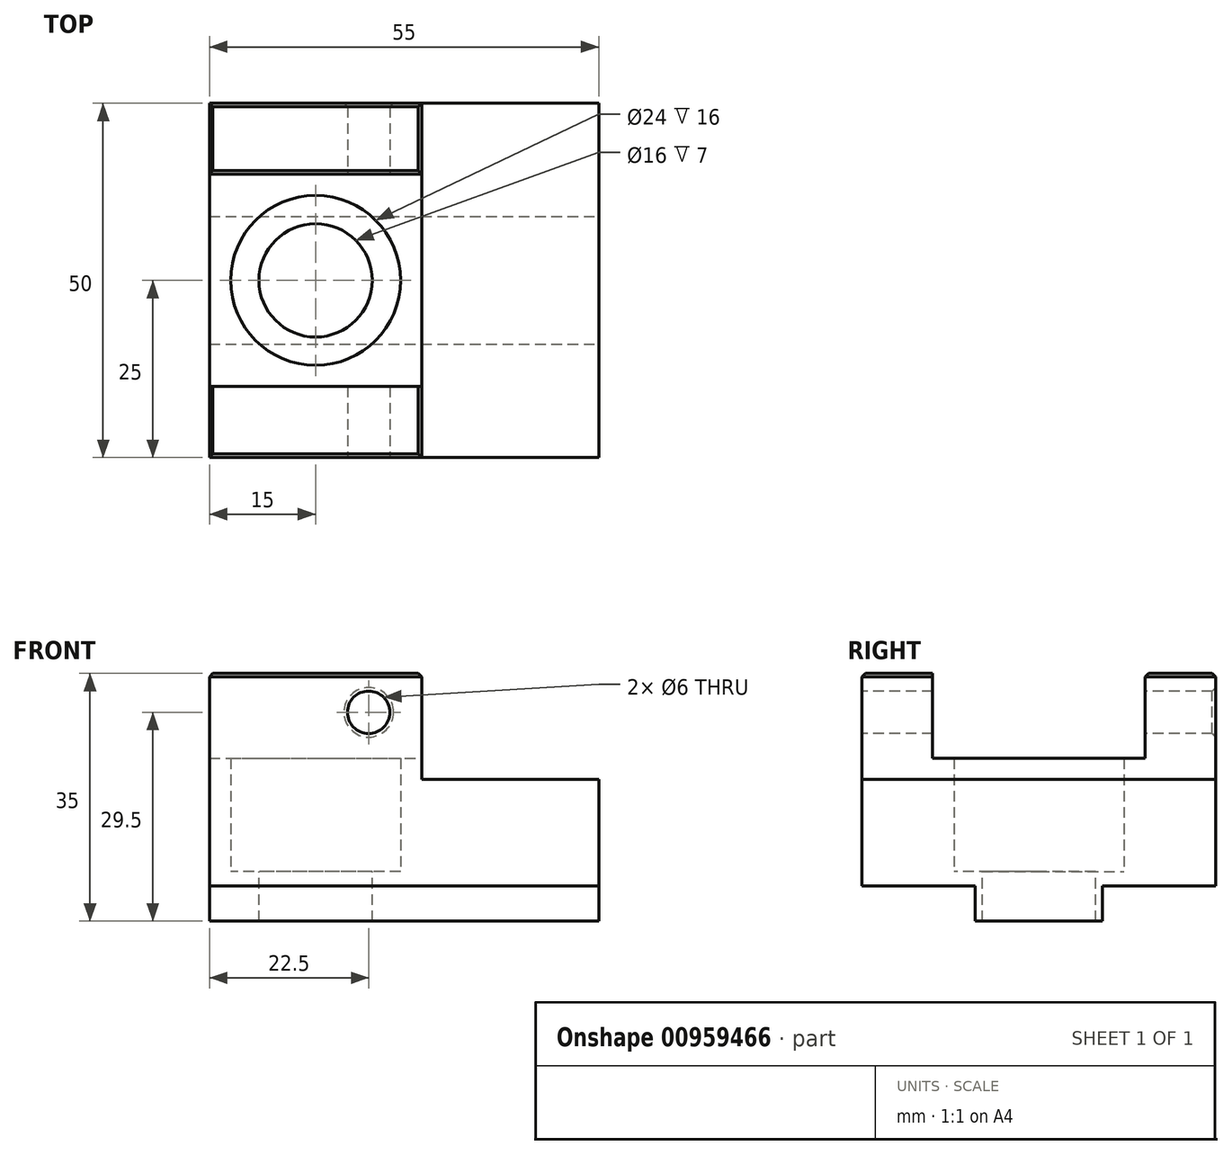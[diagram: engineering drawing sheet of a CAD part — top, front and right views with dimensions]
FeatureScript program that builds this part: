
annotation { "Feature Type Name" : "Feature", "Feature Type Description" : "" }
export const myFeature = defineFeature(function(context is Context, id is Id, definition is map)
    precondition{}
    {
        {
            var Q0;
            Q0=qCreatedBy(makeId("Top.planeOp"),FACE);
            var sketch = newSketch(context, id + "F0", { "sketchPlane" : qUnion([Q0])});
            skLineSegment(sketch, "E0.bottom", {"start": v(0, 0) * mm, "end": v(-30, 0) * mm});
            skLineSegment(sketch, "E0.top", {"start": v(0, 50) * mm, "end": v(-30, 50) * mm});
            skLineSegment(sketch, "E0.left", {"start": v(0, 0) * mm, "end": v(0, 50) * mm});
            skLineSegment(sketch, "E0.right", {"start": v(-30, 0) * mm, "end": v(-30, 50) * mm});
            skSolve(sketch);
        }
        {
            var Q0;
            Q0 = qSketchRegion(id + "F0", true);
            extrude(context, id + "F1", {"entities" : qUnion([Q0]), "depth" : 30 * mm, "offsetDistance" : 25 * mm});
        }
        {
            var Q0;
            Q0=makeQuery(id+"F1.opExtrude","SWEPT_FACE",FACE,{"disambiguationData":[OSD([sQuery(id+"F0.wireOp",EDGE,"E0.left")])]});
            var sketch = newSketch(context, id + "F2", { "sketchPlane" : qUnion([Q0])});
            skLineSegment(sketch, "E1.bottom", {"start": v(0, 0) * mm, "end": v(50, 0) * mm});
            skLineSegment(sketch, "E1.top", {"start": v(0, 15) * mm, "end": v(50, 15) * mm});
            skLineSegment(sketch, "E1.left", {"start": v(0, 0) * mm, "end": v(0, 15) * mm});
            skLineSegment(sketch, "E1.right", {"start": v(50, 0) * mm, "end": v(50, 15) * mm});
            skSolve(sketch);
        }
        {
            var Q0;
            Q0 = qSketchRegion(id + "F2", true);
            extrude(context, id + "F3", {"entities" : qUnion([Q0]), "operationType" : NewBodyOperationType.ADD, "depth" : 25 * mm, "offsetDistance" : 25 * mm});
        }
        {
            var Q0;
            Q0=makeQuery(id+"F3.boolean.opBoolean","MERGE",FACE,{"derivedFrom":[makeQuery(id+"F1.opExtrude","SWEPT_FACE",FACE,{"disambiguationData":[OSD([sQuery(id+"F0.wireOp",EDGE,"E0.bottom")])]}),makeQuery(id+"F3.opExtrude","SWEPT_FACE",FACE,{"disambiguationData":[OSD([sQuery(id+"F2.wireOp",EDGE,"E1.left")])]})]});
            var sketch = newSketch(context, id + "F4", { "sketchPlane" : qUnion([Q0])});
            skCircle(sketch, "E2", {"center": v(-7.5, 24.5) * mm, "radius": 3 * mm});
            skLineSegment(sketch, "E3", {"start": v(0, 15) * mm, "end": v(0, 30) * mm, "construction": true});
            skLineSegment(sketch, "E4", {"start": v(0, 24.5) * mm, "end": v(-30, 24.5) * mm, "construction": true});
            skSolve(sketch);
        }
        {
            var Q0;
            Q0=makeQuery(id+"F3.boolean.opBoolean","MERGE",FACE,{"derivedFrom":[makeQuery(id+"F1.opExtrude","CAP_FACE",FACE,{"disambiguationData":[OSD([sQuery(id+"F0.wireOp",EDGE,"E0.bottom"),sQuery(id+"F0.wireOp",EDGE,"E0.top"),sQuery(id+"F0.wireOp",EDGE,"E0.left"),sQuery(id+"F0.wireOp",EDGE,"E0.right")])],"isStart":true}),makeQuery(id+"F3.opExtrude","SWEPT_FACE",FACE,{"disambiguationData":[OSD([sQuery(id+"F2.wireOp",EDGE,"E1.bottom")])]})]});
            var sketch = newSketch(context, id + "F5", { "sketchPlane" : qUnion([Q0])});
            skLineSegment(sketch, "E5.bottom", {"start": v(-30, -16) * mm, "end": v(25, -16) * mm});
            skLineSegment(sketch, "E5.top", {"start": v(-30, -34) * mm, "end": v(25, -34) * mm});
            skLineSegment(sketch, "E5.left", {"start": v(-30, -16) * mm, "end": v(-30, -34) * mm});
            skLineSegment(sketch, "E5.right", {"start": v(25, -16) * mm, "end": v(25, -34) * mm});
            skLineSegment(sketch, "E6", {"start": v(-30, -25) * mm, "end": v(25, -25) * mm, "construction": true});
            skSolve(sketch);
        }
        {
            var Q0;
            Q0 = qSketchRegion(id + "F5", true);
            extrude(context, id + "F6", {"entities" : qUnion([Q0]), "operationType" : NewBodyOperationType.ADD, "depth" : 5 * mm, "offsetDistance" : 25 * mm});
        }
        {
            var Q0;
            Q0=makeQuery(id+"F4.imprint","IMPRINT",FACE,{"disambiguationData":[TD([[makeQuery(id+"F4.imprint","IMPRINT",EDGE,{"derivedFrom":sQuery(id+"F4.wireOp",EDGE,"E2")}),1.0]])]});
            extrude(context, id + "F7", {"entities" : qUnion([Q0]), "operationType" : NewBodyOperationType.REMOVE, "endBound" : BoundingType.THROUGH_ALL, "oppositeDirection" : true, "depth" : 25 * mm, "offsetDistance" : 25 * mm});
        }
        {
            var Q0;
            Q0=makeQuery(id+"F7.boolean.opBoolean","COPY",EDGE,{"derivedFrom":makeQuery(id+"F7.opExtrude","CAP_EDGE",EDGE,{"disambiguationData":[OSD([sQuery(id+"F4.wireOp",EDGE,"E2")])],"isStart":true})});
            var Q1;
            Q1=makeQuery(id+"F7.boolean.opBoolean","INTERSECT",EDGE,{"derivedFrom":[makeQuery(id+"F3.boolean.opBoolean","MERGE",FACE,{"derivedFrom":[makeQuery(id+"F1.opExtrude","SWEPT_FACE",FACE,{"disambiguationData":[OSD([sQuery(id+"F0.wireOp",EDGE,"E0.top")])]}),makeQuery(id+"F3.opExtrude","SWEPT_FACE",FACE,{"disambiguationData":[OSD([sQuery(id+"F2.wireOp",EDGE,"E1.right")])]})]}),makeQuery(id+"F7.opExtrude","SWEPT_FACE",FACE,{"disambiguationData":[OSD([sQuery(id+"F4.wireOp",EDGE,"E2")])]})]});
            chamfer(context, id + "F8", {"entities" : qUnion([Q0, Q1]), "width" : 0.5 * mm, "tangentPropagation" : true});
        }
        {
            var Q0;
            Q0=makeQuery(id+"F1.opExtrude","SWEPT_FACE",FACE,{"disambiguationData":[OSD([sQuery(id+"F0.wireOp",EDGE,"E0.left")])]});
            var sketch = newSketch(context, id + "F9", { "sketchPlane" : qUnion([Q0])});
            skLineSegment(sketch, "E7.bottom", {"start": v(10, 30) * mm, "end": v(40, 30) * mm});
            skLineSegment(sketch, "E7.top", {"start": v(10, 18) * mm, "end": v(40, 18) * mm});
            skLineSegment(sketch, "E7.left", {"start": v(10, 30) * mm, "end": v(10, 18) * mm});
            skLineSegment(sketch, "E7.right", {"start": v(40, 30) * mm, "end": v(40, 18) * mm});
            skLineSegment(sketch, "E8", {"start": v(0, 30) * mm, "end": v(10, 30) * mm, "construction": true});
            skLineSegment(sketch, "E9", {"start": v(40, 30) * mm, "end": v(50, 30) * mm, "construction": true});
            skSolve(sketch);
        }
        {
            var Q0;
            Q0 = qSketchRegion(id + "F9", true);
            extrude(context, id + "F10", {"entities" : qUnion([Q0]), "operationType" : NewBodyOperationType.REMOVE, "endBound" : BoundingType.THROUGH_ALL, "oppositeDirection" : true, "depth" : 25 * mm, "offsetDistance" : 25 * mm});
        }
        {
            var Q0;
            Q0=makeQuery(id+"F10.boolean.opBoolean","COPY",FACE,{"disambiguationData":[TD([makeQuery(id+"F1.opExtrude","SWEPT_FACE",FACE,{"disambiguationData":[OSD([sQuery(id+"F0.wireOp",EDGE,"E0.left")])]})])],"derivedFrom":makeQuery(id+"F10.opExtrude","SWEPT_FACE",FACE,{"disambiguationData":[OSD([sQuery(id+"F9.wireOp",EDGE,"E7.top")])]})});
            var sketch = newSketch(context, id + "F11", { "sketchPlane" : qUnion([Q0])});
            skCircle(sketch, "E10", {"center": v(-15, 25) * mm, "radius": 12 * mm});
            skLineSegment(sketch, "E11", {"start": v(-30, 25) * mm, "end": v(0, 25) * mm, "construction": true});
            skLineSegment(sketch, "E12", {"start": v(-15, 25) * mm, "end": v(-15, 37) * mm, "construction": true});
            skSolve(sketch);
        }
        {
            var Q0;
            Q0 = qSketchRegion(id + "F11", true);
            extrude(context, id + "F12", {"entities" : qUnion([Q0]), "operationType" : NewBodyOperationType.REMOVE, "endBound" : BoundingType.THROUGH_ALL, "depth" : 25 * mm, "offsetDistance" : 25 * mm, "hasSecondDirection" : true, "secondDirectionOppositeDirection" : true, "secondDirectionDepth" : 16 * mm});
        }
        {
            var Q0;
            {var subQ0=sQuery(id+"F0.wireOp",EDGE,"E0.right");var subQ1=sQuery(id+"F0.wireOp",EDGE,"E0.bottom");Q0=makeQuery(id+"F10.boolean.opBoolean","SPLIT",EDGE,{"disambiguationData":[TD([makeQuery(id+"F1.opExtrude","SWEPT_FACE",FACE,{"disambiguationData":[OSD([subQ1])]})])],"derivedFrom":makeQuery(id+"F1.opExtrude","CAP_EDGE",EDGE,{"disambiguationData":[OSD([subQ0])],"isStart":false})});}
            var Q1;
            Q1=makeQuery(id+"F10.boolean.opBoolean","COPY",EDGE,{"derivedFrom":makeQuery(id+"F10.opExtrude","SWEPT_EDGE",EDGE,{"disambiguationData":[OSD([sQuery(id+"F0.wireOp",EDGE,"E0.left"),sQuery(id+"F9.wireOp",EDGE,"E7.bottom"),sQuery(id+"F9.wireOp",EDGE,"E7.left")])]})});
            var Q2;
            {var subQ0=sQuery(id+"F0.wireOp",EDGE,"E0.left");var subQ1=sQuery(id+"F0.wireOp",EDGE,"E0.bottom");Q2=makeQuery(id+"F10.boolean.opBoolean","SPLIT",EDGE,{"disambiguationData":[TD([makeQuery(id+"F1.opExtrude","SWEPT_FACE",FACE,{"disambiguationData":[OSD([subQ1])]})])],"derivedFrom":makeQuery(id+"F1.opExtrude","CAP_EDGE",EDGE,{"disambiguationData":[OSD([subQ0])],"isStart":false})});}
            var Q3;
            Q3=makeQuery(id+"F1.opExtrude","CAP_EDGE",EDGE,{"disambiguationData":[OSD([sQuery(id+"F0.wireOp",EDGE,"E0.bottom")])],"isStart":false});
            var Q4;
            Q4=makeQuery(id+"F10.boolean.opBoolean","COPY",EDGE,{"derivedFrom":makeQuery(id+"F10.opExtrude","SWEPT_EDGE",EDGE,{"disambiguationData":[OSD([sQuery(id+"F0.wireOp",EDGE,"E0.left"),sQuery(id+"F9.wireOp",EDGE,"E7.bottom"),sQuery(id+"F9.wireOp",EDGE,"E7.right")])]})});
            var Q5;
            {var subQ0=sQuery(id+"F0.wireOp",EDGE,"E0.right");var subQ1=sQuery(id+"F0.wireOp",EDGE,"E0.top");Q5=makeQuery(id+"F10.boolean.opBoolean","SPLIT",EDGE,{"disambiguationData":[TD([makeQuery(id+"F1.opExtrude","SWEPT_FACE",FACE,{"disambiguationData":[OSD([subQ1])]})])],"derivedFrom":makeQuery(id+"F1.opExtrude","CAP_EDGE",EDGE,{"disambiguationData":[OSD([subQ0])],"isStart":false})});}
            var Q6;
            Q6=makeQuery(id+"F1.opExtrude","CAP_EDGE",EDGE,{"disambiguationData":[OSD([sQuery(id+"F0.wireOp",EDGE,"E0.top")])],"isStart":false});
            var Q7;
            {var subQ0=sQuery(id+"F0.wireOp",EDGE,"E0.left");var subQ1=sQuery(id+"F0.wireOp",EDGE,"E0.top");Q7=makeQuery(id+"F10.boolean.opBoolean","SPLIT",EDGE,{"disambiguationData":[TD([makeQuery(id+"F1.opExtrude","SWEPT_FACE",FACE,{"disambiguationData":[OSD([subQ1])]})])],"derivedFrom":makeQuery(id+"F1.opExtrude","CAP_EDGE",EDGE,{"disambiguationData":[OSD([subQ0])],"isStart":false})});}
            chamfer(context, id + "F13", {"entities" : qUnion([Q0, Q1, Q2, Q3, Q4, Q5, Q6, Q7]), "width" : 0.5 * mm, "tangentPropagation" : true});
        }
        {
            var Q0;
            Q0=makeQuery(id+"F12.boolean.opBoolean","COPY",FACE,{"derivedFrom":makeQuery(id+"F12.opExtrude","CAP_FACE",FACE,{"disambiguationData":[OSD([sQuery(id+"F11.wireOp",EDGE,"E10")])],"isStart":true})});
            var sketch = newSketch(context, id + "F14", { "sketchPlane" : qUnion([Q0])});
            skCircle(sketch, "E13", {"center": v(-15, 25) * mm, "radius": 8 * mm});
            skSolve(sketch);
        }
        {
            var Q0;
            Q0 = qSketchRegion(id + "F14", true);
            extrude(context, id + "F15", {"entities" : qUnion([Q0]), "operationType" : NewBodyOperationType.REMOVE, "endBound" : BoundingType.THROUGH_ALL, "oppositeDirection" : true, "depth" : 25 * mm, "offsetDistance" : 25 * mm});
        }
    });
